# Revit family: Rapid_80_Geräteeinbaukanal_Stahlblech-Systeme_Kanalbreite_170mm_Kanalhöhe_70_und_90_aysymmetrisch
name_source: partatom
category: Generic Models
revit_build: Autodesk Revit 2015 (Build: 20140606_1530(x64)
units: mm (PartAtom-declared; Revit-internal decimal feet)

## types (3) — shared parameters
Lenght = 2000 mm  [stored 6.56168 ft]
Manufacturer = OBO Bettermann
Material = Steel AISI 1008 91 HR
URL = http://www.obo-bettermann.com

## per-type parameters (varying)
| type | Article Type | GTIN | Height | Manufacturer Art.No. |
| GS-A90170RW | GS-A90170RW | 4012195663317 | 90 mm  [stored 0.295276 ft] | 6277900 |
| GS-A70170RW | GS-A70170RW | 4012195662945 | 70 mm  [stored 0.229659 ft] | 6277800 |
| GS-A70170RW2 | GS-A70170RW | 4012195740612 | 70 mm  [stored 0.229659 ft] | 6277807 |

note: [stored X ft] marks values corroborated as IEEE doubles in the binary element streams (Revit-internal decimal feet)

## geometry (parser evidence)
native form markers: Sweep x2
no freeform markers — native parametric forms only
